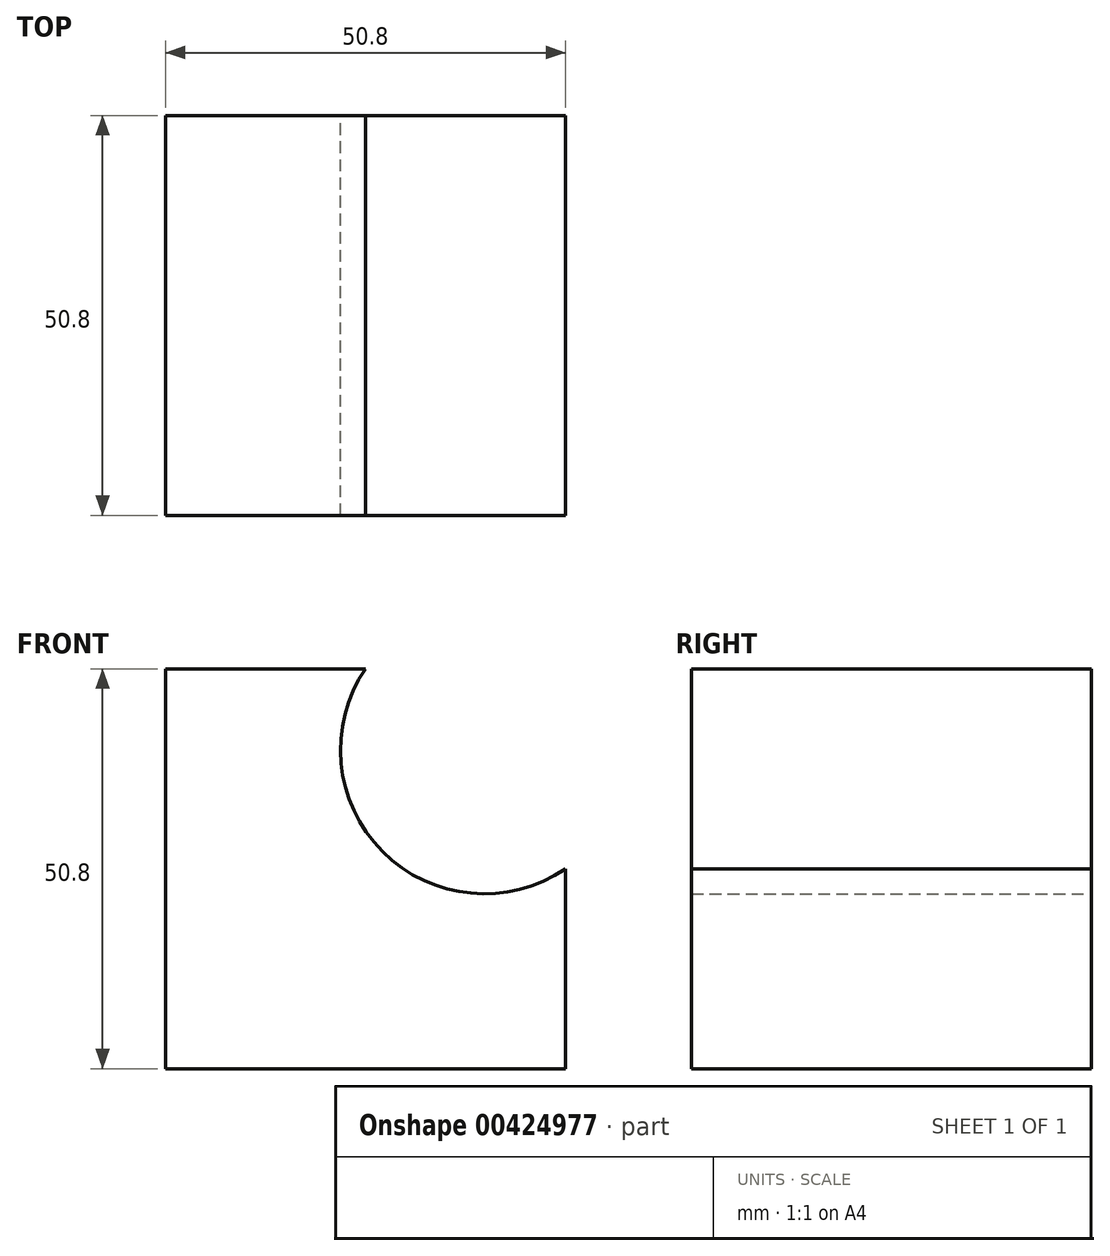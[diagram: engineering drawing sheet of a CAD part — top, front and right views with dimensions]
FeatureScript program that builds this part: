
annotation { "Feature Type Name" : "Feature", "Feature Type Description" : "" }
export const myFeature = defineFeature(function(context is Context, id is Id, definition is map)
    precondition{}
    {
        {
            var Q0;
            Q0=qCreatedBy(makeId("Front.planeOp"),FACE);
            var sketch = newSketch(context, id + "F0", { "sketchPlane" : qUnion([Q0])});
            skLineSegment(sketch, "E0", {"start": v(0, 25.4) * mm, "end": v(0, 0) * mm});
            skLineSegment(sketch, "E1", {"start": v(0, 0) * mm, "end": v(-50.8, 0) * mm});
            skLineSegment(sketch, "E2", {"start": v(-50.8, 0) * mm, "end": v(-50.8, 50.8) * mm});
            skLineSegment(sketch, "E3", {"start": v(-50.8, 50.8) * mm, "end": v(-25.4, 50.8) * mm});
            skArc(sketch, "E4", {"start": v(-25.4, 50.8) * mm, "mid": v(-23.23, 27.57) * mm, "end": v(0, 25.4) * mm});
            skSolve(sketch);
        }
        {
            var Q0;
            Q0=makeQuery(id+"F0.imprint","IMPRINT",FACE,{"disambiguationData":[TD([[makeQuery(id+"F0.imprint","IMPRINT",EDGE,{"derivedFrom":sQuery(id+"F0.wireOp",EDGE,"E0")}),-1.0]])]});
            extrude(context, id + "F1", {"entities" : qUnion([Q0]), "depth" : 50.8 * mm});
        }
    });
